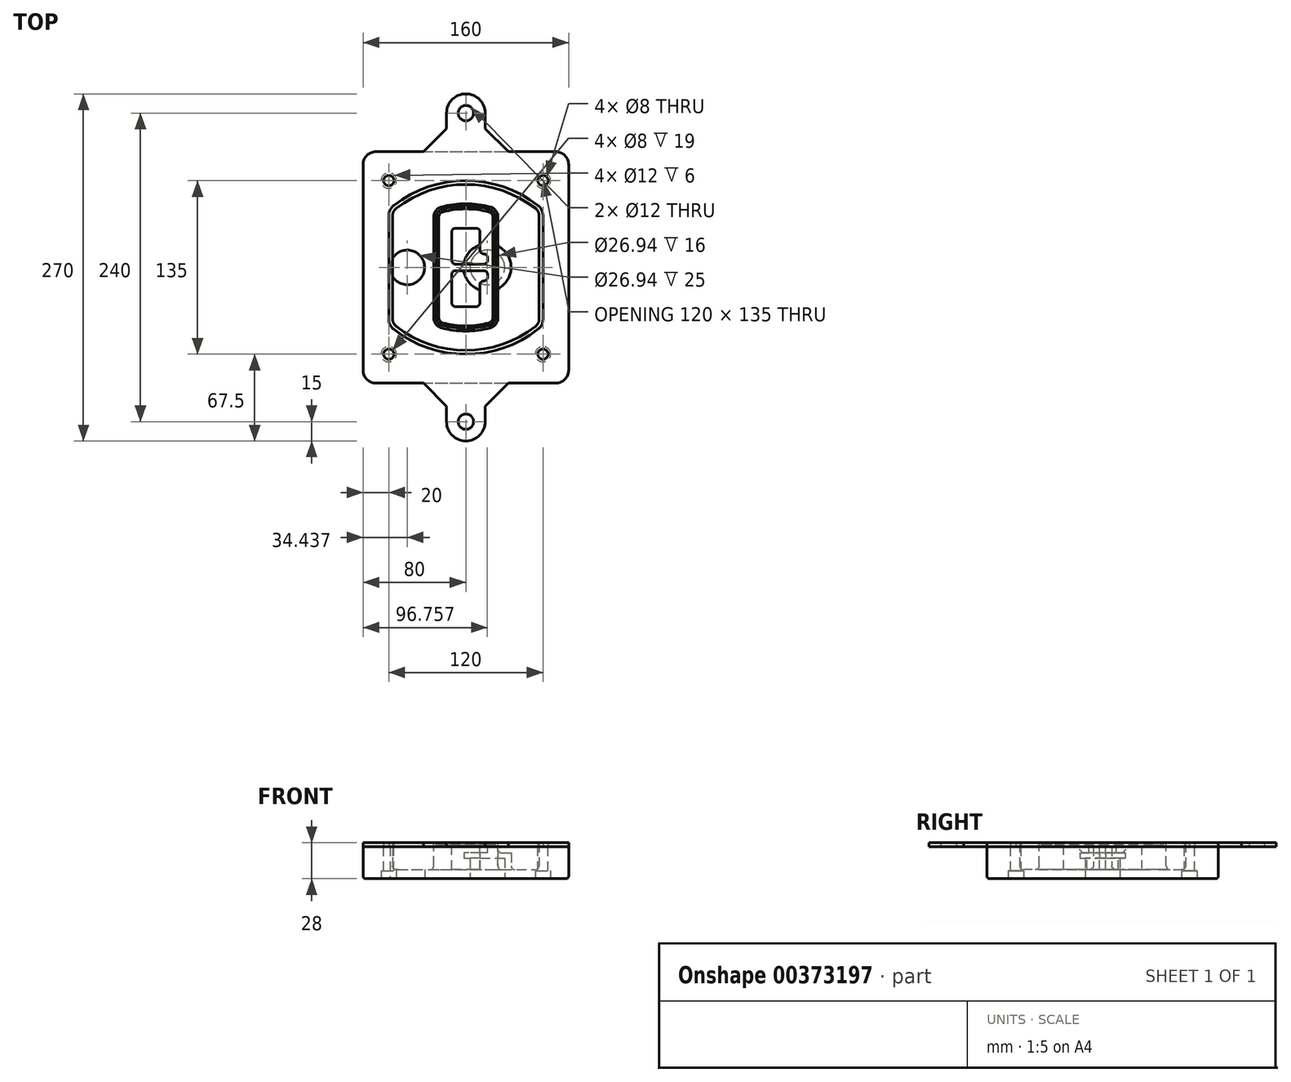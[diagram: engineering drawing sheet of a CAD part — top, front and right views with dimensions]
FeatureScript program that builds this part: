
annotation { "Feature Type Name" : "Feature", "Feature Type Description" : "" }
export const myFeature = defineFeature(function(context is Context, id is Id, definition is map)
    precondition{}
    {
        {
            var Q0;
            Q0=qCreatedBy(makeId("Top.planeOp"),FACE);
            var sketch = newSketch(context, id + "F0", { "sketchPlane" : qUnion([Q0])});
            skPoint(sketch, "E0.rect.middle", {"position": v(0, 0) * mm});
            skLineSegment(sketch, "E1.bottom", {"start": v(-70, -90) * mm, "end": v(70, -90) * mm});
            skLineSegment(sketch, "E1.top", {"start": v(-70, 90) * mm, "end": v(70, 90) * mm});
            skLineSegment(sketch, "E1.left", {"start": v(-80, -80) * mm, "end": v(-80, 80) * mm});
            skLineSegment(sketch, "E1.right", {"start": v(80, -80) * mm, "end": v(80, 80) * mm});
            skLineSegment(sketch, "E2", {"start": v(-80, 90) * mm, "end": v(80, -90) * mm, "construction": true});
            skLineSegment(sketch, "E3", {"start": v(80, 90) * mm, "end": v(-80, -90) * mm, "construction": true});
            skCircle(sketch, "E4", {"center": v(-60, 67.5) * mm, "radius": 4 * mm});
            skCircle(sketch, "E5", {"center": v(60, 67.5) * mm, "radius": 4 * mm});
            skCircle(sketch, "E6", {"center": v(60, -67.5) * mm, "radius": 4 * mm});
            skCircle(sketch, "E7", {"center": v(-60, -67.5) * mm, "radius": 4 * mm});
            skLineSegment(sketch, "E8", {"start": v(-60, 67.5) * mm, "end": v(60, 67.5) * mm, "construction": true});
            skLineSegment(sketch, "E9", {"start": v(60, 67.5) * mm, "end": v(60, -67.5) * mm, "construction": true});
            skLineSegment(sketch, "E10", {"start": v(60, -67.5) * mm, "end": v(-60, -67.5) * mm, "construction": true});
            skLineSegment(sketch, "E11", {"start": v(-60, -67.5) * mm, "end": v(-60, 67.5) * mm, "construction": true});
            skLineSegment(sketch, "E12", {"start": v(-60, 40.3) * mm, "end": v(-60, -40.3) * mm});
            skLineSegment(sketch, "E13", {"start": v(60, 40.3) * mm, "end": v(60, -40.3) * mm});
            skArc(sketch, "E14", {"start": v(56.15, 48.18) * mm, "mid": v(0, 67.5) * mm, "end": v(-56.15, 48.18) * mm});
            skArc(sketch, "E15", {"start": v(-56.15, -48.18) * mm, "mid": v(0, -67.5) * mm, "end": v(56.15, -48.18) * mm});
            skLineSegment(sketch, "E16", {"start": v(-60, 0) * mm, "end": v(60, 0) * mm, "construction": true});
            skPoint(sketch, "E17.visualSharp", {"position": v(-60, -45) * mm});
            skArc(sketch, "E17.filletArc", {"start": v(-60, -40.3) * mm, "mid": v(-58.99, -44.68) * mm, "end": v(-56.15, -48.18) * mm});
            skPoint(sketch, "E18.visualSharp", {"position": v(-60, 45) * mm});
            skArc(sketch, "E18.filletArc", {"start": v(-56.15, 48.18) * mm, "mid": v(-58.99, 44.68) * mm, "end": v(-60, 40.3) * mm});
            skPoint(sketch, "E19.visualSharp", {"position": v(60, 45) * mm});
            skArc(sketch, "E19.filletArc", {"start": v(60, 40.3) * mm, "mid": v(58.99, 44.68) * mm, "end": v(56.15, 48.18) * mm});
            skPoint(sketch, "E20.visualSharp", {"position": v(60, -45) * mm});
            skArc(sketch, "E20.filletArc", {"start": v(56.15, -48.18) * mm, "mid": v(58.99, -44.68) * mm, "end": v(60, -40.3) * mm});
            skPoint(sketch, "E21.visualSharp", {"position": v(-80, 90) * mm});
            skArc(sketch, "E21.filletArc", {"start": v(-70, 90) * mm, "mid": v(-77.07, 87.07) * mm, "end": v(-80, 80) * mm});
            skPoint(sketch, "E22.visualSharp", {"position": v(80, 90) * mm});
            skArc(sketch, "E22.filletArc", {"start": v(80, 80) * mm, "mid": v(77.07, 87.07) * mm, "end": v(70, 90) * mm});
            skPoint(sketch, "E23.visualSharp", {"position": v(80, -90) * mm});
            skArc(sketch, "E23.filletArc", {"start": v(70, -90) * mm, "mid": v(77.07, -87.07) * mm, "end": v(80, -80) * mm});
            skPoint(sketch, "E24.visualSharp", {"position": v(-80, -90) * mm});
            skArc(sketch, "E24.filletArc", {"start": v(-80, -80) * mm, "mid": v(-77.07, -87.07) * mm, "end": v(-70, -90) * mm});
            skArc(sketch, "E25.0", {"start": v(57, 40.3) * mm, "mid": v(56.3, 43.36) * mm, "end": v(54.3, 45.81) * mm});
            skLineSegment(sketch, "E25.1", {"start": v(57, 40.3) * mm, "end": v(57, -40.3) * mm});
            skArc(sketch, "E25.2", {"start": v(54.3, -45.81) * mm, "mid": v(56.3, -43.36) * mm, "end": v(57, -40.3) * mm});
            skArc(sketch, "E25.3", {"start": v(-54.3, -45.81) * mm, "mid": v(0, -64.5) * mm, "end": v(54.3, -45.81) * mm});
            skArc(sketch, "E25.4", {"start": v(-57, -40.3) * mm, "mid": v(-56.3, -43.36) * mm, "end": v(-54.3, -45.81) * mm});
            skArc(sketch, "E25.5", {"start": v(54.3, 45.81) * mm, "mid": v(0, 64.5) * mm, "end": v(-54.3, 45.81) * mm});
            skLineSegment(sketch, "E25.6", {"start": v(-57, 40.3) * mm, "end": v(-57, -40.3) * mm});
            skArc(sketch, "E25.7", {"start": v(-54.3, 45.81) * mm, "mid": v(-56.3, 43.36) * mm, "end": v(-57, 40.3) * mm});
            skArc(sketch, "E26.0", {"start": v(-58.62, 51.33) * mm, "mid": v(-62.58, 46.43) * mm, "end": v(-64, 40.3) * mm});
            skArc(sketch, "E26.1", {"start": v(58.62, 51.33) * mm, "mid": v(0, 71.5) * mm, "end": v(-58.62, 51.33) * mm});
            skArc(sketch, "E26.2", {"start": v(64, 40.3) * mm, "mid": v(62.58, 46.43) * mm, "end": v(58.62, 51.33) * mm});
            skLineSegment(sketch, "E26.3", {"start": v(64, 40.3) * mm, "end": v(64, -40.3) * mm});
            skArc(sketch, "E26.4", {"start": v(58.62, -51.33) * mm, "mid": v(62.58, -46.43) * mm, "end": v(64, -40.3) * mm});
            skLineSegment(sketch, "E26.5", {"start": v(-64, 40.3) * mm, "end": v(-64, -40.3) * mm});
            skArc(sketch, "E26.6", {"start": v(-58.62, -51.33) * mm, "mid": v(0, -71.5) * mm, "end": v(58.62, -51.33) * mm});
            skArc(sketch, "E26.7", {"start": v(-64, -40.3) * mm, "mid": v(-62.58, -46.43) * mm, "end": v(-58.62, -51.33) * mm});
            skSolve(sketch);
        }
        {
            var Q0;
            Q0=makeQuery(id+"F0.imprint","IMPRINT",FACE,{"disambiguationData":[TD([[makeQuery(id+"F0.imprint","IMPRINT",EDGE,{"derivedFrom":sQuery(id+"F0.wireOp",EDGE,"E1.bottom")}),1.0]])]});
            var Q1;
            Q1=makeQuery(id+"F0.imprint","IMPRINT",FACE,{"disambiguationData":[TD([[makeQuery(id+"F0.imprint","IMPRINT",EDGE,{"derivedFrom":sQuery(id+"F0.wireOp",EDGE,"E12")}),1.0]])]});
            var Q2;
            Q2=makeQuery(id+"F0.imprint","IMPRINT",FACE,{"disambiguationData":[TD([[makeQuery(id+"F0.imprint","IMPRINT",EDGE,{"derivedFrom":sQuery(id+"F0.wireOp",EDGE,"E25.0")}),1.0]])]});
            var Q3;
            Q3=makeQuery(id+"F0.imprint","IMPRINT",FACE,{"disambiguationData":[TD([[makeQuery(id+"F0.imprint","IMPRINT",EDGE,{"derivedFrom":sQuery(id+"F0.wireOp",EDGE,"E12")}),-1.0]])]});
            extrude(context, id + "F1", {"entities" : qUnion([Q0, Q1, Q2, Q3]), "oppositeDirection" : true, "depth" : 25 * mm});
        }
        {
            var Q0;
            Q0=makeQuery(id+"F0.imprint","IMPRINT",FACE,{"disambiguationData":[TD([[makeQuery(id+"F0.imprint","IMPRINT",EDGE,{"derivedFrom":sQuery(id+"F0.wireOp",EDGE,"E12")}),1.0]])]});
            extrude(context, id + "F2", {"entities" : qUnion([Q0]), "operationType" : NewBodyOperationType.ADD, "depth" : 3 * mm});
        }
        {
            var Q0;
            Q0=makeQuery(id+"F0.imprint","IMPRINT",FACE,{"disambiguationData":[TD([[makeQuery(id+"F0.imprint","IMPRINT",EDGE,{"derivedFrom":sQuery(id+"F0.wireOp",EDGE,"E25.0")}),1.0]])]});
            extrude(context, id + "F3", {"entities" : qUnion([Q0]), "operationType" : NewBodyOperationType.REMOVE, "oppositeDirection" : true, "depth" : 18 * mm});
        }
        {
            var Q0;
            Q0=makeQuery(id+"F2.opExtrude","CAP_FACE",FACE,{"disambiguationData":[OSD([sQuery(id+"F0.wireOp",EDGE,"E12"),sQuery(id+"F0.wireOp",EDGE,"E13"),sQuery(id+"F0.wireOp",EDGE,"E14"),sQuery(id+"F0.wireOp",EDGE,"E15"),sQuery(id+"F0.wireOp",EDGE,"E17.filletArc"),sQuery(id+"F0.wireOp",EDGE,"E18.filletArc"),sQuery(id+"F0.wireOp",EDGE,"E19.filletArc"),sQuery(id+"F0.wireOp",EDGE,"E20.filletArc"),sQuery(id+"F0.wireOp",EDGE,"E25.0"),sQuery(id+"F0.wireOp",EDGE,"E25.1"),sQuery(id+"F0.wireOp",EDGE,"E25.2"),sQuery(id+"F0.wireOp",EDGE,"E25.3"),sQuery(id+"F0.wireOp",EDGE,"E25.4"),sQuery(id+"F0.wireOp",EDGE,"E25.5"),sQuery(id+"F0.wireOp",EDGE,"E25.6"),sQuery(id+"F0.wireOp",EDGE,"E25.7")])],"isStart":false});
            var sketch = newSketch(context, id + "F4", { "sketchPlane" : qUnion([Q0])});
            skArc(sketch, "E27.0", {"start": v(-19.08, -46.97) * mm, "mid": v(0, -49.5) * mm, "end": v(19.08, -46.97) * mm});
            skArc(sketch, "E28.0", {"start": v(19.08, 46.97) * mm, "mid": v(0, 49.5) * mm, "end": v(-19.08, 46.97) * mm});
            skLineSegment(sketch, "E29", {"start": v(-25, 39.25) * mm, "end": v(-25, -39.25) * mm});
            skLineSegment(sketch, "E30", {"start": v(25, 39.25) * mm, "end": v(25, -39.25) * mm});
            skLineSegment(sketch, "E31", {"start": v(-25, 45.1) * mm, "end": v(25, 45.1) * mm, "construction": true});
            skLineSegment(sketch, "E32", {"start": v(-25, -45.1) * mm, "end": v(25, -45.1) * mm, "construction": true});
            skPoint(sketch, "E33.visualSharp", {"position": v(-25, 45.1) * mm});
            skArc(sketch, "E33.filletArc", {"start": v(-19.08, 46.97) * mm, "mid": v(-23.35, 44.11) * mm, "end": v(-25, 39.25) * mm});
            skPoint(sketch, "E34.visualSharp", {"position": v(25, 45.1) * mm});
            skArc(sketch, "E34.filletArc", {"start": v(25, 39.25) * mm, "mid": v(23.35, 44.11) * mm, "end": v(19.08, 46.97) * mm});
            skPoint(sketch, "E35.visualSharp", {"position": v(25, -45.1) * mm});
            skArc(sketch, "E35.filletArc", {"start": v(19.08, -46.97) * mm, "mid": v(23.35, -44.11) * mm, "end": v(25, -39.25) * mm});
            skPoint(sketch, "E36.visualSharp", {"position": v(-25, -45.1) * mm});
            skArc(sketch, "E36.filletArc", {"start": v(-25, -39.25) * mm, "mid": v(-23.35, -44.11) * mm, "end": v(-19.08, -46.97) * mm});
            skArc(sketch, "E37.0", {"start": v(54.3, 45.81) * mm, "mid": v(0, 64.5) * mm, "end": v(-54.3, 45.81) * mm});
            skArc(sketch, "E37.1", {"start": v(-54.3, 45.81) * mm, "mid": v(-56.3, 43.36) * mm, "end": v(-57, 40.3) * mm});
            skLineSegment(sketch, "E37.2", {"start": v(-57, 40.3) * mm, "end": v(-57, -40.3) * mm});
            skArc(sketch, "E37.3", {"start": v(-57, -40.3) * mm, "mid": v(-56.3, -43.36) * mm, "end": v(-54.3, -45.81) * mm});
            skArc(sketch, "E37.4", {"start": v(-54.3, -45.81) * mm, "mid": v(0, -64.5) * mm, "end": v(54.3, -45.81) * mm});
            skArc(sketch, "E37.5", {"start": v(54.3, -45.81) * mm, "mid": v(56.3, -43.36) * mm, "end": v(57, -40.3) * mm});
            skLineSegment(sketch, "E37.6", {"start": v(57, 40.3) * mm, "end": v(57, -40.3) * mm});
            skArc(sketch, "E37.7", {"start": v(57, 40.3) * mm, "mid": v(56.3, 43.36) * mm, "end": v(54.3, 45.81) * mm});
            skLineSegment(sketch, "E38.0", {"start": v(23, 39.25) * mm, "end": v(23, -39.25) * mm});
            skArc(sketch, "E38.1", {"start": v(18.56, -45.04) * mm, "mid": v(21.76, -42.9) * mm, "end": v(23, -39.25) * mm});
            skArc(sketch, "E38.2", {"start": v(-18.56, -45.04) * mm, "mid": v(0, -47.5) * mm, "end": v(18.56, -45.04) * mm});
            skArc(sketch, "E38.3", {"start": v(-23, -39.25) * mm, "mid": v(-21.76, -42.9) * mm, "end": v(-18.56, -45.04) * mm});
            skLineSegment(sketch, "E38.4", {"start": v(-23, 39.25) * mm, "end": v(-23, -39.25) * mm});
            skArc(sketch, "E38.5", {"start": v(23, 39.25) * mm, "mid": v(21.76, 42.9) * mm, "end": v(18.56, 45.04) * mm});
            skArc(sketch, "E38.6", {"start": v(-18.56, 45.04) * mm, "mid": v(-21.76, 42.9) * mm, "end": v(-23, 39.25) * mm});
            skArc(sketch, "E38.7", {"start": v(18.56, 45.04) * mm, "mid": v(0, 47.5) * mm, "end": v(-18.56, 45.04) * mm});
            skArc(sketch, "E39.0", {"start": v(21, 39.25) * mm, "mid": v(20.18, 41.68) * mm, "end": v(18.04, 43.1) * mm});
            skLineSegment(sketch, "E39.1", {"start": v(21, 39.25) * mm, "end": v(21, -39.25) * mm});
            skArc(sketch, "E39.2", {"start": v(18.04, -43.1) * mm, "mid": v(20.18, -41.68) * mm, "end": v(21, -39.25) * mm});
            skArc(sketch, "E39.3", {"start": v(-18.04, -43.1) * mm, "mid": v(0, -45.5) * mm, "end": v(18.04, -43.1) * mm});
            skArc(sketch, "E39.4", {"start": v(-21, -39.25) * mm, "mid": v(-20.18, -41.68) * mm, "end": v(-18.04, -43.1) * mm});
            skArc(sketch, "E39.5", {"start": v(18.04, 43.1) * mm, "mid": v(0, 45.5) * mm, "end": v(-18.04, 43.1) * mm});
            skLineSegment(sketch, "E39.6", {"start": v(-21, 39.25) * mm, "end": v(-21, -39.25) * mm});
            skArc(sketch, "E39.7", {"start": v(-18.04, 43.1) * mm, "mid": v(-20.18, 41.68) * mm, "end": v(-21, 39.25) * mm});
            skLineSegment(sketch, "E40", {"start": v(-25, 0) * mm, "end": v(25, 0) * mm, "construction": true});
            skLineSegment(sketch, "E41", {"start": v(-11, 5.5) * mm, "end": v(-11, 27.5) * mm});
            skLineSegment(sketch, "E42", {"start": v(-8, 30.5) * mm, "end": v(8, 30.5) * mm});
            skLineSegment(sketch, "E43", {"start": v(11, 27.5) * mm, "end": v(11, 13.5) * mm});
            skLineSegment(sketch, "E44", {"start": v(14, 10.5) * mm, "end": v(14, 10.5) * mm});
            skLineSegment(sketch, "E45", {"start": v(17, 7.5) * mm, "end": v(17, 5.5) * mm});
            skLineSegment(sketch, "E46", {"start": v(14, 2.5) * mm, "end": v(-8, 2.5) * mm});
            skPoint(sketch, "E47.visualSharp", {"position": v(-11, 30.5) * mm});
            skArc(sketch, "E47.filletArc", {"start": v(-8, 30.5) * mm, "mid": v(-10.12, 29.62) * mm, "end": v(-11, 27.5) * mm});
            skPoint(sketch, "E48.visualSharp", {"position": v(11, 30.5) * mm});
            skArc(sketch, "E48.filletArc", {"start": v(11, 27.5) * mm, "mid": v(10.12, 29.62) * mm, "end": v(8, 30.5) * mm});
            skPoint(sketch, "E49.visualSharp", {"position": v(11, 10.5) * mm});
            skArc(sketch, "E49.filletArc", {"start": v(11, 13.5) * mm, "mid": v(11.88, 11.38) * mm, "end": v(14, 10.5) * mm});
            skPoint(sketch, "E50.visualSharp", {"position": v(17, 10.5) * mm});
            skArc(sketch, "E50.filletArc", {"start": v(17, 7.5) * mm, "mid": v(16.12, 9.62) * mm, "end": v(14, 10.5) * mm});
            skPoint(sketch, "E51.visualSharp", {"position": v(17, 2.5) * mm});
            skArc(sketch, "E51.filletArc", {"start": v(14, 2.5) * mm, "mid": v(16.12, 3.38) * mm, "end": v(17, 5.5) * mm});
            skPoint(sketch, "E52.visualSharp", {"position": v(-11, 2.5) * mm});
            skArc(sketch, "E52.filletArc", {"start": v(-11, 5.5) * mm, "mid": v(-10.12, 3.38) * mm, "end": v(-8, 2.5) * mm});
            skLineSegment(sketch, "E53.0.MirrorCS", {"start": v(14, -2.5) * mm, "end": v(-8, -2.5) * mm});
            skArc(sketch, "E54.0.MirrorCS", {"start": v(-11, -5.5) * mm, "mid": v(-10.12, -3.38) * mm, "end": v(-8, -2.5) * mm});
            skLineSegment(sketch, "E55.0.MirrorCS", {"start": v(-11, -5.5) * mm, "end": v(-11, -27.5) * mm});
            skArc(sketch, "E56.0.MirrorCS", {"start": v(-8, -30.5) * mm, "mid": v(-10.12, -29.62) * mm, "end": v(-11, -27.5) * mm});
            skLineSegment(sketch, "E57.0.MirrorCS", {"start": v(-8, -30.5) * mm, "end": v(8, -30.5) * mm});
            skArc(sketch, "E58.0.MirrorCS", {"start": v(11, -27.5) * mm, "mid": v(10.12, -29.62) * mm, "end": v(8, -30.5) * mm});
            skLineSegment(sketch, "E59.0.MirrorCS", {"start": v(11, -27.5) * mm, "end": v(11, -13.5) * mm});
            skArc(sketch, "E60.0.MirrorCS", {"start": v(11, -13.5) * mm, "mid": v(11.88, -11.38) * mm, "end": v(14, -10.5) * mm});
            skArc(sketch, "E61.0.MirrorCS", {"start": v(17, -7.5) * mm, "mid": v(16.12, -9.62) * mm, "end": v(14, -10.5) * mm});
            skLineSegment(sketch, "E62.0.MirrorCS", {"start": v(17, -7.5) * mm, "end": v(17, -5.5) * mm});
            skArc(sketch, "E63.0.MirrorCS", {"start": v(14, -2.5) * mm, "mid": v(16.12, -3.38) * mm, "end": v(17, -5.5) * mm});
            skSolve(sketch);
        }
        {
            var Q0;
            Q0=makeQuery(id+"F4.imprint","IMPRINT",FACE,{"disambiguationData":[TD([[makeQuery(id+"F4.imprint","IMPRINT",EDGE,{"derivedFrom":sQuery(id+"F4.wireOp",EDGE,"E27.0")}),1.0]])]});
            var Q1;
            Q1=makeQuery(id+"F4.imprint","IMPRINT",FACE,{"disambiguationData":[TD([[makeQuery(id+"F4.imprint","IMPRINT",EDGE,{"derivedFrom":sQuery(id+"F4.wireOp",EDGE,"E38.0")}),-1.0]])]});
            var Q2;
            Q2=makeQuery(id+"F4.imprint","IMPRINT",FACE,{"disambiguationData":[TD([[makeQuery(id+"F4.imprint","IMPRINT",EDGE,{"derivedFrom":sQuery(id+"F4.wireOp",EDGE,"E39.0")}),1.0]])]});
            extrude(context, id + "F5", {"entities" : qUnion([Q0, Q1, Q2]), "operationType" : NewBodyOperationType.ADD, "endBound" : BoundingType.UP_TO_NEXT, "oppositeDirection" : true, "depth" : 25 * mm});
        }
        {
            var Q0;
            Q0=makeQuery(id+"F4.imprint","IMPRINT",FACE,{"disambiguationData":[TD([[makeQuery(id+"F4.imprint","IMPRINT",EDGE,{"derivedFrom":sQuery(id+"F4.wireOp",EDGE,"E38.0")}),-1.0]])]});
            extrude(context, id + "F6", {"entities" : qUnion([Q0]), "operationType" : NewBodyOperationType.REMOVE, "oppositeDirection" : true, "depth" : 2 * mm});
        }
        {
            var Q0;
            Q0=makeQuery(id+"F1.opExtrude","CAP_FACE",FACE,{"disambiguationData":[OSD([sQuery(id+"F0.wireOp",EDGE,"E1.bottom"),sQuery(id+"F0.wireOp",EDGE,"E1.top"),sQuery(id+"F0.wireOp",EDGE,"E1.left"),sQuery(id+"F0.wireOp",EDGE,"E1.right"),sQuery(id+"F0.wireOp",EDGE,"E4"),sQuery(id+"F0.wireOp",EDGE,"E5"),sQuery(id+"F0.wireOp",EDGE,"E6"),sQuery(id+"F0.wireOp",EDGE,"E7"),sQuery(id+"F0.wireOp",EDGE,"E21.filletArc"),sQuery(id+"F0.wireOp",EDGE,"E22.filletArc"),sQuery(id+"F0.wireOp",EDGE,"E23.filletArc"),sQuery(id+"F0.wireOp",EDGE,"E24.filletArc")])],"isStart":false});
            var sketch = newSketch(context, id + "F7", { "sketchPlane" : qUnion([Q0])});
            skCircle(sketch, "E64", {"center": v(16.76, 0) * mm, "radius": 13.47 * mm});
            skCircle(sketch, "E65", {"center": v(-45.56, 0) * mm, "radius": 13.47 * mm});
            skLineSegment(sketch, "E66", {"start": v(80, 0) * mm, "end": v(-80, 0) * mm});
            skCircle(sketch, "E67", {"center": v(16.76, 0) * mm, "radius": 18.47 * mm});
            skCircle(sketch, "E68", {"center": v(60, -67.5) * mm, "radius": 6 * mm});
            skCircle(sketch, "E69", {"center": v(-60, -67.5) * mm, "radius": 6 * mm});
            skCircle(sketch, "E70", {"center": v(-60, 67.5) * mm, "radius": 6 * mm});
            skCircle(sketch, "E71", {"center": v(60, 67.5) * mm, "radius": 6 * mm});
            skSolve(sketch);
        }
        {
            var Q0;
            {var subQ1=sQuery(id+"F7.wireOp",EDGE,"E66");var subQ4=sQuery(id+"F7.wireOp",EDGE,"E64");var subQ6=makeQuery(id+"F7.imprint","INTERSECT",VERTEX,{"disambiguationData":[OD(0.0)],"derivedFrom":[subQ4,subQ1]});Q0=makeQuery(id+"F7.imprint","IMPRINT",FACE,{"disambiguationData":[TD([[makeQuery(id+"F7.imprint","IMPRINT",EDGE,{"disambiguationData":[TD([[subQ6,-1.0]])],"derivedFrom":subQ4}),-1.0]])]});}
            var Q1;
            {var subQ0=sQuery(id+"F7.wireOp",EDGE,"E66");var subQ1=sQuery(id+"F7.wireOp",EDGE,"E64");var subQ3=makeQuery(id+"F7.imprint","INTERSECT",VERTEX,{"disambiguationData":[OD(0.0)],"derivedFrom":[subQ1,subQ0]});Q1=makeQuery(id+"F7.imprint","IMPRINT",FACE,{"disambiguationData":[TD([[makeQuery(id+"F7.imprint","IMPRINT",EDGE,{"disambiguationData":[TD([[subQ3,-1.0]])],"derivedFrom":subQ1}),1.0]])]});}
            var Q2;
            {var subQ0=sQuery(id+"F7.wireOp",EDGE,"E66");var subQ1=sQuery(id+"F7.wireOp",EDGE,"E64");var subQ3=makeQuery(id+"F7.imprint","INTERSECT",VERTEX,{"disambiguationData":[OD(0.0)],"derivedFrom":[subQ1,subQ0]});Q2=makeQuery(id+"F7.imprint","IMPRINT",FACE,{"disambiguationData":[TD([[makeQuery(id+"F7.imprint","IMPRINT",EDGE,{"disambiguationData":[TD([[subQ3,1.0]])],"derivedFrom":subQ1}),1.0]])]});}
            var Q3;
            {var subQ1=sQuery(id+"F7.wireOp",EDGE,"E66");var subQ4=sQuery(id+"F7.wireOp",EDGE,"E64");var subQ6=makeQuery(id+"F7.imprint","INTERSECT",VERTEX,{"disambiguationData":[OD(0.0)],"derivedFrom":[subQ4,subQ1]});Q3=makeQuery(id+"F7.imprint","IMPRINT",FACE,{"disambiguationData":[TD([[makeQuery(id+"F7.imprint","IMPRINT",EDGE,{"disambiguationData":[TD([[subQ6,1.0]])],"derivedFrom":subQ4}),-1.0]])]});}
            extrude(context, id + "F8", {"entities" : qUnion([Q0, Q1, Q2, Q3]), "operationType" : NewBodyOperationType.ADD, "oppositeDirection" : true, "depth" : 20 * mm});
        }
        {
            var Q0;
            {var subQ0=sQuery(id+"F7.wireOp",EDGE,"E66");var subQ1=sQuery(id+"F7.wireOp",EDGE,"E64");var subQ3=makeQuery(id+"F7.imprint","INTERSECT",VERTEX,{"disambiguationData":[OD(0.0)],"derivedFrom":[subQ1,subQ0]});Q0=makeQuery(id+"F7.imprint","IMPRINT",FACE,{"disambiguationData":[TD([[makeQuery(id+"F7.imprint","IMPRINT",EDGE,{"disambiguationData":[TD([[subQ3,-1.0]])],"derivedFrom":subQ1}),1.0]])]});}
            var Q1;
            {var subQ0=sQuery(id+"F7.wireOp",EDGE,"E66");var subQ1=sQuery(id+"F7.wireOp",EDGE,"E64");var subQ3=makeQuery(id+"F7.imprint","INTERSECT",VERTEX,{"disambiguationData":[OD(0.0)],"derivedFrom":[subQ1,subQ0]});Q1=makeQuery(id+"F7.imprint","IMPRINT",FACE,{"disambiguationData":[TD([[makeQuery(id+"F7.imprint","IMPRINT",EDGE,{"disambiguationData":[TD([[subQ3,1.0]])],"derivedFrom":subQ1}),1.0]])]});}
            extrude(context, id + "F9", {"entities" : qUnion([Q0, Q1]), "operationType" : NewBodyOperationType.REMOVE, "oppositeDirection" : true, "depth" : 16 * mm});
        }
        {
            var Q0;
            {var subQ0=sQuery(id+"F7.wireOp",EDGE,"E66");var subQ1=sQuery(id+"F7.wireOp",EDGE,"E65");var subQ3=makeQuery(id+"F7.imprint","INTERSECT",VERTEX,{"disambiguationData":[OD(0.0)],"derivedFrom":[subQ1,subQ0]});Q0=makeQuery(id+"F7.imprint","IMPRINT",FACE,{"disambiguationData":[TD([[makeQuery(id+"F7.imprint","IMPRINT",EDGE,{"disambiguationData":[TD([[subQ3,-1.0]])],"derivedFrom":subQ1}),1.0]])]});}
            var Q1;
            {var subQ0=sQuery(id+"F7.wireOp",EDGE,"E66");var subQ1=sQuery(id+"F7.wireOp",EDGE,"E65");var subQ3=makeQuery(id+"F7.imprint","INTERSECT",VERTEX,{"disambiguationData":[OD(0.0)],"derivedFrom":[subQ1,subQ0]});Q1=makeQuery(id+"F7.imprint","IMPRINT",FACE,{"disambiguationData":[TD([[makeQuery(id+"F7.imprint","IMPRINT",EDGE,{"disambiguationData":[TD([[subQ3,1.0]])],"derivedFrom":subQ1}),1.0]])]});}
            extrude(context, id + "F10", {"entities" : qUnion([Q0, Q1]), "operationType" : NewBodyOperationType.REMOVE, "oppositeDirection" : true, "depth" : 25 * mm});
        }
        {
            var Q0;
            Q0=makeQuery(id+"F7.imprint","IMPRINT",FACE,{"disambiguationData":[TD([[makeQuery(id+"F7.imprint","IMPRINT",EDGE,{"derivedFrom":sQuery(id+"F7.wireOp",EDGE,"E68")}),1.0]])]});
            var Q1;
            Q1=makeQuery(id+"F7.imprint","IMPRINT",FACE,{"disambiguationData":[TD([[makeQuery(id+"F7.imprint","IMPRINT",EDGE,{"derivedFrom":makeQuery(id+"F1.opExtrude","CAP_EDGE",EDGE,{"disambiguationData":[OSD([sQuery(id+"F0.wireOp",EDGE,"E5")])],"isStart":false})}),-1.0]])]});
            var Q2;
            Q2=makeQuery(id+"F7.imprint","IMPRINT",FACE,{"disambiguationData":[TD([[makeQuery(id+"F7.imprint","IMPRINT",EDGE,{"derivedFrom":sQuery(id+"F7.wireOp",EDGE,"E69")}),1.0]])]});
            var Q3;
            Q3=makeQuery(id+"F7.imprint","IMPRINT",FACE,{"disambiguationData":[TD([[makeQuery(id+"F7.imprint","IMPRINT",EDGE,{"derivedFrom":makeQuery(id+"F1.opExtrude","CAP_EDGE",EDGE,{"disambiguationData":[OSD([sQuery(id+"F0.wireOp",EDGE,"E4")])],"isStart":false})}),-1.0]])]});
            var Q4;
            Q4=makeQuery(id+"F7.imprint","IMPRINT",FACE,{"disambiguationData":[TD([[makeQuery(id+"F7.imprint","IMPRINT",EDGE,{"derivedFrom":sQuery(id+"F7.wireOp",EDGE,"E70")}),1.0]])]});
            var Q5;
            Q5=makeQuery(id+"F7.imprint","IMPRINT",FACE,{"disambiguationData":[TD([[makeQuery(id+"F7.imprint","IMPRINT",EDGE,{"derivedFrom":makeQuery(id+"F1.opExtrude","CAP_EDGE",EDGE,{"disambiguationData":[OSD([sQuery(id+"F0.wireOp",EDGE,"E7")])],"isStart":false})}),-1.0]])]});
            var Q6;
            Q6=makeQuery(id+"F7.imprint","IMPRINT",FACE,{"disambiguationData":[TD([[makeQuery(id+"F7.imprint","IMPRINT",EDGE,{"derivedFrom":sQuery(id+"F7.wireOp",EDGE,"E71")}),1.0]])]});
            var Q7;
            Q7=makeQuery(id+"F7.imprint","IMPRINT",FACE,{"disambiguationData":[TD([[makeQuery(id+"F7.imprint","IMPRINT",EDGE,{"derivedFrom":makeQuery(id+"F1.opExtrude","CAP_EDGE",EDGE,{"disambiguationData":[OSD([sQuery(id+"F0.wireOp",EDGE,"E6")])],"isStart":false})}),-1.0]])]});
            extrude(context, id + "F11", {"entities" : qUnion([Q0, Q1, Q2, Q3, Q4, Q5, Q6, Q7]), "operationType" : NewBodyOperationType.REMOVE, "oppositeDirection" : true, "depth" : 6 * mm});
        }
        {
            var Q0;
            Q0=makeQuery(id+"F9.boolean.opBoolean","COPY",FACE,{"derivedFrom":makeQuery(id+"F9.opExtrude","CAP_FACE",FACE,{"disambiguationData":[OSD([sQuery(id+"F7.wireOp",EDGE,"E64")])],"isStart":false})});
            var sketch = newSketch(context, id + "F12", { "sketchPlane" : qUnion([Q0])});
            skArc(sketch, "E72.0", {"start": v(11, 17.55) * mm, "mid": v(2.57, 11.82) * mm, "end": v(-1.54, 2.5) * mm});
            skArc(sketch, "E72.1", {"start": v(-1.54, -2.5) * mm, "mid": v(2.57, -11.82) * mm, "end": v(11, -17.55) * mm});
            skLineSegment(sketch, "E73", {"start": v(-1.54, -2.5) * mm, "end": v(14, -2.5) * mm});
            skLineSegment(sketch, "E74.0", {"start": v(14, 2.5) * mm, "end": v(-1.54, 2.5) * mm});
            skArc(sketch, "E74.1", {"start": v(14, 2.5) * mm, "mid": v(16.12, 3.38) * mm, "end": v(17, 5.5) * mm});
            skLineSegment(sketch, "E74.2", {"start": v(17, 7.5) * mm, "end": v(17, 5.5) * mm});
            skArc(sketch, "E74.3", {"start": v(17, 7.5) * mm, "mid": v(16.12, 9.62) * mm, "end": v(14, 10.5) * mm});
            skArc(sketch, "E74.4", {"start": v(11, 13.5) * mm, "mid": v(11.88, 11.38) * mm, "end": v(14, 10.5) * mm});
            skLineSegment(sketch, "E74.5", {"start": v(11, 17.55) * mm, "end": v(11, 13.5) * mm});
            skLineSegment(sketch, "E74.7", {"start": v(14, -2.5) * mm, "end": v(-1.54, -2.5) * mm});
            skArc(sketch, "E74.8", {"start": v(14, -2.5) * mm, "mid": v(16.12, -3.38) * mm, "end": v(17, -5.5) * mm});
            skLineSegment(sketch, "E74.9", {"start": v(17, -7.5) * mm, "end": v(17, -5.5) * mm});
            skArc(sketch, "E74.10", {"start": v(17, -7.5) * mm, "mid": v(16.12, -9.62) * mm, "end": v(14, -10.5) * mm});
            skArc(sketch, "E74.11", {"start": v(11, -13.5) * mm, "mid": v(11.88, -11.38) * mm, "end": v(14, -10.5) * mm});
            skLineSegment(sketch, "E74.12", {"start": v(11, -17.55) * mm, "end": v(11, -13.5) * mm});
            skPoint(sketch, "E75.orphan", {"position": v(11, -27.5) * mm});
            skPoint(sketch, "E76.orphan", {"position": v(-8, -2.5) * mm});
            skPoint(sketch, "E77.orphan", {"position": v(-8, 2.5) * mm});
            skPoint(sketch, "E78.orphan", {"position": v(11, 27.5) * mm});
            skSolve(sketch);
        }
        {
            var Q0;
            {var subQ7=sQuery(id+"F12.wireOp",EDGE,"E72.0");var subQ14=sQuery(id+"F12.wireOp",EDGE,"E72.1");var subQ16=sQuery(id+"F12.wireOp",EDGE,"E74.1");var subQ18=sQuery(id+"F12.wireOp",EDGE,"E74.8");Q0=qUnion([makeQuery(id+"F12.imprint","IMPRINT",FACE,{"disambiguationData":[TD([[makeQuery(id+"F12.imprint","IMPRINT",EDGE,{"derivedFrom":subQ7}),1.0]])]}),makeQuery(id+"F12.imprint","IMPRINT",FACE,{"disambiguationData":[TD([[makeQuery(id+"F12.imprint","IMPRINT",EDGE,{"derivedFrom":subQ14}),1.0]])]}),makeQuery(id+"F12.imprint","IMPRINT",FACE,{"disambiguationData":[TD([[makeQuery(id+"F12.imprint","IMPRINT",EDGE,{"derivedFrom":subQ16}),1.0]])]}),makeQuery(id+"F12.imprint","IMPRINT",FACE,{"disambiguationData":[TD([[makeQuery(id+"F12.imprint","IMPRINT",EDGE,{"derivedFrom":subQ18}),-1.0]])]})]);}
            var Q1;
            Q1=makeQuery(id+"F5.boolean.opBoolean","SPLIT",FACE,{"disambiguationData":[TD([makeQuery(id+"F5.opExtrude","SWEPT_FACE",FACE,{"disambiguationData":[OSD([sQuery(id+"F4.wireOp",EDGE,"E41")])]})])],"derivedFrom":makeQuery(id+"F3.boolean.opBoolean","COPY",FACE,{"derivedFrom":makeQuery(id+"F3.opExtrude","CAP_FACE",FACE,{"disambiguationData":[OSD([sQuery(id+"F0.wireOp",EDGE,"E25.0"),sQuery(id+"F0.wireOp",EDGE,"E25.1"),sQuery(id+"F0.wireOp",EDGE,"E25.2"),sQuery(id+"F0.wireOp",EDGE,"E25.3"),sQuery(id+"F0.wireOp",EDGE,"E25.4"),sQuery(id+"F0.wireOp",EDGE,"E25.5"),sQuery(id+"F0.wireOp",EDGE,"E25.6"),sQuery(id+"F0.wireOp",EDGE,"E25.7")])],"isStart":false})})});
            extrude(context, id + "F13", {"entities" : qUnion([Q0]), "operationType" : NewBodyOperationType.REMOVE, "endBound" : BoundingType.UP_TO_SURFACE, "endBoundEntityFace" : qUnion([Q1]), "depth" : 25 * mm});
        }
        {
            var Q0;
            Q0=makeQuery(id+"F3.boolean.opBoolean","COPY",EDGE,{"derivedFrom":makeQuery(id+"F3.opExtrude","CAP_EDGE",EDGE,{"disambiguationData":[OSD([sQuery(id+"F0.wireOp",EDGE,"E25.6")])],"isStart":false})});
            var Q1;
            Q1=makeQuery(id+"F8.boolean.opBoolean","INTERSECT",EDGE,{"derivedFrom":[makeQuery(id+"F5.opExtrude","SWEPT_FACE",FACE,{"disambiguationData":[OSD([sQuery(id+"F4.wireOp",EDGE,"E30")])]}),makeQuery(id+"F8.opExtrude","CAP_FACE",FACE,{"disambiguationData":[OSD([sQuery(id+"F7.wireOp",EDGE,"E67")])],"isStart":false})]});
            var Q2;
            Q2=makeQuery(id+"F8.boolean.opBoolean","INTERSECT",EDGE,{"disambiguationData":[OD(1.0)],"derivedFrom":[makeQuery(id+"F5.opExtrude","SWEPT_FACE",FACE,{"disambiguationData":[OSD([sQuery(id+"F4.wireOp",EDGE,"E30")])]}),makeQuery(id+"F8.opExtrude","SWEPT_FACE",FACE,{"disambiguationData":[OSD([sQuery(id+"F7.wireOp",EDGE,"E67")])]})]});
            var Q3;
            {var subQ0=sQuery(id+"F4.wireOp",EDGE,"E30");Q3=makeQuery(id+"F8.boolean.opBoolean","SPLIT",EDGE,{"disambiguationData":[TD([makeQuery(id+"F5.opExtrude","SWEPT_FACE",FACE,{"disambiguationData":[OSD([sQuery(id+"F4.wireOp",EDGE,"E35.filletArc")])]})])],"derivedFrom":makeQuery(id+"F5.opExtrude","CAP_EDGE",EDGE,{"disambiguationData":[OSD([subQ0])],"isStart":false})});}
            var Q4;
            {var subQ0=sQuery(id+"F0.wireOp",EDGE,"E25.7");var subQ1=sQuery(id+"F0.wireOp",EDGE,"E25.1");var subQ2=sQuery(id+"F0.wireOp",EDGE,"E25.6");var subQ3=sQuery(id+"F0.wireOp",EDGE,"E25.5");var subQ4=sQuery(id+"F0.wireOp",EDGE,"E25.4");var subQ5=sQuery(id+"F0.wireOp",EDGE,"E25.0");var subQ6=sQuery(id+"F0.wireOp",EDGE,"E25.2");var subQ7=sQuery(id+"F0.wireOp",EDGE,"E25.3");Q4=makeQuery(id+"F8.boolean.opBoolean","INTERSECT",EDGE,{"derivedFrom":[makeQuery(id+"F5.boolean.opBoolean","SPLIT",FACE,{"disambiguationData":[TD([makeQuery(id+"F2.opExtrude","SWEPT_FACE",FACE,{"disambiguationData":[OSD([subQ5])]})])],"derivedFrom":makeQuery(id+"F3.boolean.opBoolean","COPY",FACE,{"derivedFrom":makeQuery(id+"F3.opExtrude","CAP_FACE",FACE,{"disambiguationData":[OSD([subQ5,subQ1,subQ6,subQ7,subQ4,subQ3,subQ2,subQ0])],"isStart":false})})}),makeQuery(id+"F8.opExtrude","SWEPT_FACE",FACE,{"disambiguationData":[OSD([sQuery(id+"F7.wireOp",EDGE,"E67")])]})]});}
            var Q5;
            Q5=makeQuery(id+"F8.boolean.opBoolean","INTERSECT",EDGE,{"disambiguationData":[OD(0.0)],"derivedFrom":[makeQuery(id+"F5.opExtrude","SWEPT_FACE",FACE,{"disambiguationData":[OSD([sQuery(id+"F4.wireOp",EDGE,"E30")])]}),makeQuery(id+"F8.opExtrude","SWEPT_FACE",FACE,{"disambiguationData":[OSD([sQuery(id+"F7.wireOp",EDGE,"E67")])]})]});
            fillet(context, id + "F14", {"entities" : qUnion([Q0, Q1, Q2, Q3, Q4, Q5]), "radius" : 3 * mm, "tangentPropagation" : true, "allowEdgeOverflow" : false});
        }
        {
            var Q0;
            Q0=makeQuery(id+"F1.opExtrude","CAP_EDGE",EDGE,{"disambiguationData":[OSD([sQuery(id+"F0.wireOp",EDGE,"E1.bottom")])],"isStart":false});
            fillet(context, id + "F15", {"entities" : qUnion([Q0]), "radius" : 2 * mm, "tangentPropagation" : true, "allowEdgeOverflow" : false});
        }
        {
            var Q0;
            {var subQ0=sQuery(id+"F0.wireOp",EDGE,"E21.filletArc");var subQ1=sQuery(id+"F0.wireOp",EDGE,"E7");var subQ2=sQuery(id+"F0.wireOp",EDGE,"E6");var subQ3=sQuery(id+"F0.wireOp",EDGE,"E5");var subQ4=sQuery(id+"F0.wireOp",EDGE,"E4");var subQ5=sQuery(id+"F0.wireOp",EDGE,"E22.filletArc");var subQ6=sQuery(id+"F0.wireOp",EDGE,"E1.bottom");var subQ7=sQuery(id+"F0.wireOp",EDGE,"E1.right");var subQ8=sQuery(id+"F0.wireOp",EDGE,"E1.top");var subQ9=sQuery(id+"F0.wireOp",EDGE,"E1.left");var subQ10=sQuery(id+"F0.wireOp",EDGE,"E23.filletArc");var subQ11=sQuery(id+"F0.wireOp",EDGE,"E24.filletArc");Q0=makeQuery(id+"F2.boolean.opBoolean","SPLIT",FACE,{"disambiguationData":[TD([makeQuery(id+"F1.opExtrude","SWEPT_FACE",FACE,{"disambiguationData":[OSD([subQ6])]})])],"derivedFrom":makeQuery(id+"F1.opExtrude","CAP_FACE",FACE,{"disambiguationData":[OSD([subQ6,subQ8,subQ9,subQ7,subQ4,subQ3,subQ2,subQ1,subQ0,subQ5,subQ10,subQ11])],"isStart":true})});}
            var sketch = newSketch(context, id + "F16", { "sketchPlane" : qUnion([Q0])});
            skLineSegment(sketch, "E79", {"start": v(0, 90) * mm, "end": v(0, 120) * mm, "construction": true});
            skCircle(sketch, "E80", {"center": v(0, 120) * mm, "radius": 6 * mm});
            skLineSegment(sketch, "E81", {"start": v(-33, 90) * mm, "end": v(-15, 108) * mm});
            skLineSegment(sketch, "E82", {"start": v(15, 108) * mm, "end": v(33, 90) * mm});
            skLineSegment(sketch, "E83", {"start": v(15, 108) * mm, "end": v(15, 120) * mm});
            skLineSegment(sketch, "E84", {"start": v(-15, 108) * mm, "end": v(-15, 120) * mm});
            skArc(sketch, "E85", {"start": v(15, 120) * mm, "mid": v(0, 135) * mm, "end": v(-15, 120) * mm});
            skLineSegment(sketch, "E86", {"start": v(-95.62, 0) * mm, "end": v(98.97, 0) * mm, "construction": true});
            skPoint(sketch, "E86.endSnap0", {"position": v(80, 0) * mm});
            skLineSegment(sketch, "E87.MirrorCS", {"start": v(-33, -90) * mm, "end": v(-15, -108) * mm});
            skLineSegment(sketch, "E88.MirrorCS", {"start": v(0, -90) * mm, "end": v(0, -120) * mm, "construction": true});
            skArc(sketch, "E89.MirrorCS", {"start": v(15, -120) * mm, "mid": v(0, -135) * mm, "end": v(-15, -120) * mm});
            skLineSegment(sketch, "E90.MirrorCS", {"start": v(15, -108) * mm, "end": v(15, -120) * mm});
            skLineSegment(sketch, "E91.MirrorCS", {"start": v(-15, -108) * mm, "end": v(-15, -120) * mm});
            skLineSegment(sketch, "E92.MirrorCS", {"start": v(15, -108) * mm, "end": v(33, -90) * mm});
            skCircle(sketch, "E93.MirrorC", {"center": v(0, -120) * mm, "radius": 6 * mm});
            skSolve(sketch);
        }
        {
            var Q0;
            Q0=makeQuery(id+"F16.imprint","IMPRINT",FACE,{"disambiguationData":[TD([[makeQuery(id+"F16.imprint","IMPRINT",EDGE,{"derivedFrom":sQuery(id+"F16.wireOp",EDGE,"E80")}),-1.0]])]});
            var Q1;
            Q1=makeQuery(id+"F16.imprint","IMPRINT",FACE,{"disambiguationData":[TD([[makeQuery(id+"F16.imprint","IMPRINT",EDGE,{"derivedFrom":makeQuery(id+"F1.opExtrude","CAP_EDGE",EDGE,{"disambiguationData":[OSD([sQuery(id+"F0.wireOp",EDGE,"E1.left")])],"isStart":true})}),-1.0]])]});
            var Q2;
            {var subQ0=sQuery(id+"F16.wireOp",EDGE,"E87.MirrorCS");Q2=makeQuery(id+"F16.imprint","IMPRINT",FACE,{"disambiguationData":[TD([[makeQuery(id+"F16.imprint","IMPRINT",EDGE,{"derivedFrom":subQ0}),1.0]])]});}
            var Q3;
            Q3=makeQuery(id+"F2.opExtrude","CAP_FACE",FACE,{"disambiguationData":[OSD([sQuery(id+"F0.wireOp",EDGE,"E12"),sQuery(id+"F0.wireOp",EDGE,"E13"),sQuery(id+"F0.wireOp",EDGE,"E14"),sQuery(id+"F0.wireOp",EDGE,"E15"),sQuery(id+"F0.wireOp",EDGE,"E17.filletArc"),sQuery(id+"F0.wireOp",EDGE,"E18.filletArc"),sQuery(id+"F0.wireOp",EDGE,"E19.filletArc"),sQuery(id+"F0.wireOp",EDGE,"E20.filletArc"),sQuery(id+"F0.wireOp",EDGE,"E25.0"),sQuery(id+"F0.wireOp",EDGE,"E25.1"),sQuery(id+"F0.wireOp",EDGE,"E25.2"),sQuery(id+"F0.wireOp",EDGE,"E25.3"),sQuery(id+"F0.wireOp",EDGE,"E25.4"),sQuery(id+"F0.wireOp",EDGE,"E25.5"),sQuery(id+"F0.wireOp",EDGE,"E25.6"),sQuery(id+"F0.wireOp",EDGE,"E25.7")])],"isStart":false});
            extrude(context, id + "F17", {"entities" : qUnion([Q0, Q1, Q2]), "endBound" : BoundingType.UP_TO_SURFACE, "endBoundEntityFace" : qUnion([Q3]), "depth" : 25 * mm});
        }
    });
